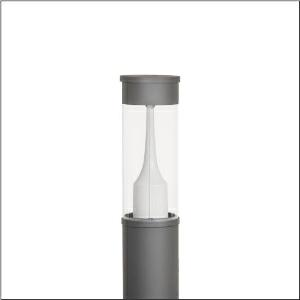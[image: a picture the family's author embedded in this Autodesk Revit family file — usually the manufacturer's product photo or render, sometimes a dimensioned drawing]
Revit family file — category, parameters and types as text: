
# Revit family: city-light_120_iq___pl1_2s_5xa5285jf14h_c322
name_source: partatom
category: Lighting Fixtures
units: mm (PartAtom-declared; Revit-internal decimal feet)

## family parameters
Cut with Voids When Loaded = No
Host = Face
Light Source = No
Part Type = Normal
Room Calculation Point = No
Round Connector Dimension = Use Diameter
Shared = No

## types (1)
- --- (1 x LED, 2970 lm, 19.3 W, 3000K)
    Apparent Load = 19 VA
    CIE Flux Codes = 23 62 94 96 100
    Color Rendering = 70
    Color Temperature = 3000K
    Default Elevation = 1800 mm
    Description = City-Light 120 iQ, bollard luminaire, Module 540 iQ-SR, primary light control with 3 zone facetted reflector, of plastic, silver coated, highly specular, structured, primary optical cover: cover, of PMMA, transparent, light distribution: PL1.2s, primary light characteristic: symmetric, LED, High Power LED, rated luminous flux: 2.970lm, luminous efficacy: 154lm/W, light colour: 730, colour temperature: 3000K, control gear: ECG iQ, control: Auto-Match, Temp-Guard, Lumen-Switch, Night-Set, Smart-Wire, Light-Fading, Desk-Remote (wireless, voltage-free reading and setting of iQ features in the workshop via application-optimized NFC function/RFID function), optimised constant luminous flux control (CLO 2.0), Street-Remote, presetting dimming logarithmic, with terminal, 6-pole, max. 2.5mm², mains connection: 230..240V, AC, 50/60Hz, start of lifetime: 19W, end of service life: 21W, reduction: 10W, luminaire housing, cylindrical, of extruded aluminium section, coated, Siteco® metallic grey (DB 702S), length: 1.200mm, diameter: 200mm, Module 540 iQ-SR, traffic white (RAL 9016), equipment: standard, protection rating (complete): IP54, insulation class (complete): insulation class II (safety insulation), certification: CE, ENEC, VDE, packaging unit: 1 piece

Light Distribution: PL1.2s
    Height = 500 mm
    Lamp = 1 x LED
    Lamp Light Flux = 2970 lm
    Lamp Power = 19.3 W
    Lamp count = 1
    Length = 200 mm  [stored 0.656168 ft]
    Luminous efficacy = 154 lm/W
    Manufacturer = Siteco
    ModVariant = No
    Model = 5XA5285JF14H
    Mounting Place = Floor
    Mounting Type = Freestanding
    Number of Poles = 1
    OnlyDefault = Yes
    Power Factor = 1
    Product Name = City-Light 120 iQ | PL1.2s
    Product group = bollard luminaire
    ProductGroupID = 1304
    Protection Class = Protection class II
    Protection Degree = IP 54
    RLX_Detail_Level = 1
    RLX_Emergency_Light_Flux = 0 lm
    RLX_Emergency_Type = 0
    RLX_Emergency_Type_DB = No
    RlxData = <blob elided: 30317 chars, md5=e3f2bf77>
    Socket = socket
    Standby Power = 0 W
    System Light Flux = 2970 lm
    System Power = 19 W
    Type Comments = factory setting: luminous flux: 100 % | dim-lin: 254 | 403 mA
    Type Image = l_1006922.jpg
    URL = http://relux.com
    VarID = @adj_094761
    Voltage = 0 V
    Weight = 0.00 kg
    Width = 0 mm  [stored 0 ft]

note: [stored X ft] marks values corroborated as IEEE doubles in the binary element streams (Revit-internal decimal feet)

## geometry (parser evidence)
native form markers: Blend x4, Sweep x11
no freeform markers — native parametric forms only
